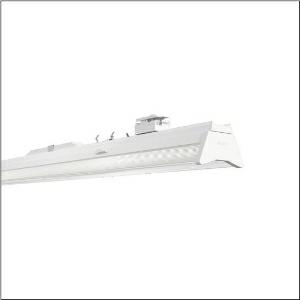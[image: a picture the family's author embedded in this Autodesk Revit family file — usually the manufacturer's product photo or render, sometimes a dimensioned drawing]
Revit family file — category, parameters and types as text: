
# Revit family: licross_r__11_performance_mo_51tm167n485g_4c90
name_source: partatom
category: Lighting Fixtures
units: mm (PartAtom-declared; Revit-internal decimal feet)

## family parameters
Cut with Voids When Loaded = No
Host = Face
Light Source = No
Part Type = Normal
Room Calculation Point = No
Round Connector Dimension = Use Diameter
Shared = No

## types (1)
- Licross® 11 Performance MO (1 x LED, 8840 lm, 48.6 W, 4000K)
    Apparent Load = 49 VA
    CIE Flux Codes = 66 88 96 79 100
    Color Rendering = 80
    Color Temperature = 4000K
    Default Elevation = 1800 mm
    Description = Licross® 11 Performance MO, luminaire insert, of sheet steel, galvanised, coil coated, white, length: 1.500mm, width: 120mm, height: 123mm, LED rated luminous flux: 8.840lm, light colour: 840, control gear: ON/OFF, with plug, 3-pole, with phase selection, mains connection: 220..240V, AC, 50/60Hz, rated input power: 49W, halogen-free wiring, primary light control with lens, of plastic, primary optical cover: cover, of PMMA, light emission: direct/indirect distribution, primary light characteristic: symmetric, protection rating (complete): IP40, insulation class (complete): insulation class I (protective earthing), certification: CE, ENEC, VDE, UKCA, protection symbol: D if used in an environment without relevant dust loads with corresponding accessories, impact resistance: IK06, permissible ambient temperature for indoor applications: -25..+35°C, corresponds to IFS (International Featured Standards) requirements for safety and quality in the food industry, reducing of maximum allowable ambient temperature of 5°C with ceiling mounting, LABS conformity tested according to VDMA 24364:2018-05, packaging unit: 1 piece
    Height = 114 mm
    Lamp = 1 x LED
    Lamp Light Flux = 8840 lm
    Lamp Power = 48.6 W
    Lamp count = 1
    Length = 1500 mm
    Luminous efficacy = 182 lm/W
    Manufacturer = Siteco
    ModVariant = No
    Model = 51TM167N485G
    Mounting Place = Ceiling
    Mounting Type = Pendant
    Number of Poles = 1
    OnlyDefault = Yes
    Power Factor = 1
    Product Name = Licross® 11 Performance MO
    Product group = luminaire insert
    ProductGroupID = 902
    Protection Class = Protection class I
    Protection Degree = IP 40
    RLX_Detail_Level = 1
    RLX_Emergency_Light_Flux = 0 lm
    RLX_Emergency_Type = 0
    RLX_Emergency_Type_DB = No
    RlxData = <blob elided: 30405 chars, md5=b70c5312>
    Socket = socket
    Standby Power = 0 W
    System Light Flux = 8840 lm
    System Power = 49 W
    Type Comments = Product without accessories
    Type Image = l_1256138.jpg
    URL = http://relux.com
    VarID = ---
    Voltage = 0 V
    Weight = 0.00 kg
    Width = 120 mm

## geometry (parser evidence)
native form markers: Blend x4, Sweep x11
no freeform markers — native parametric forms only
